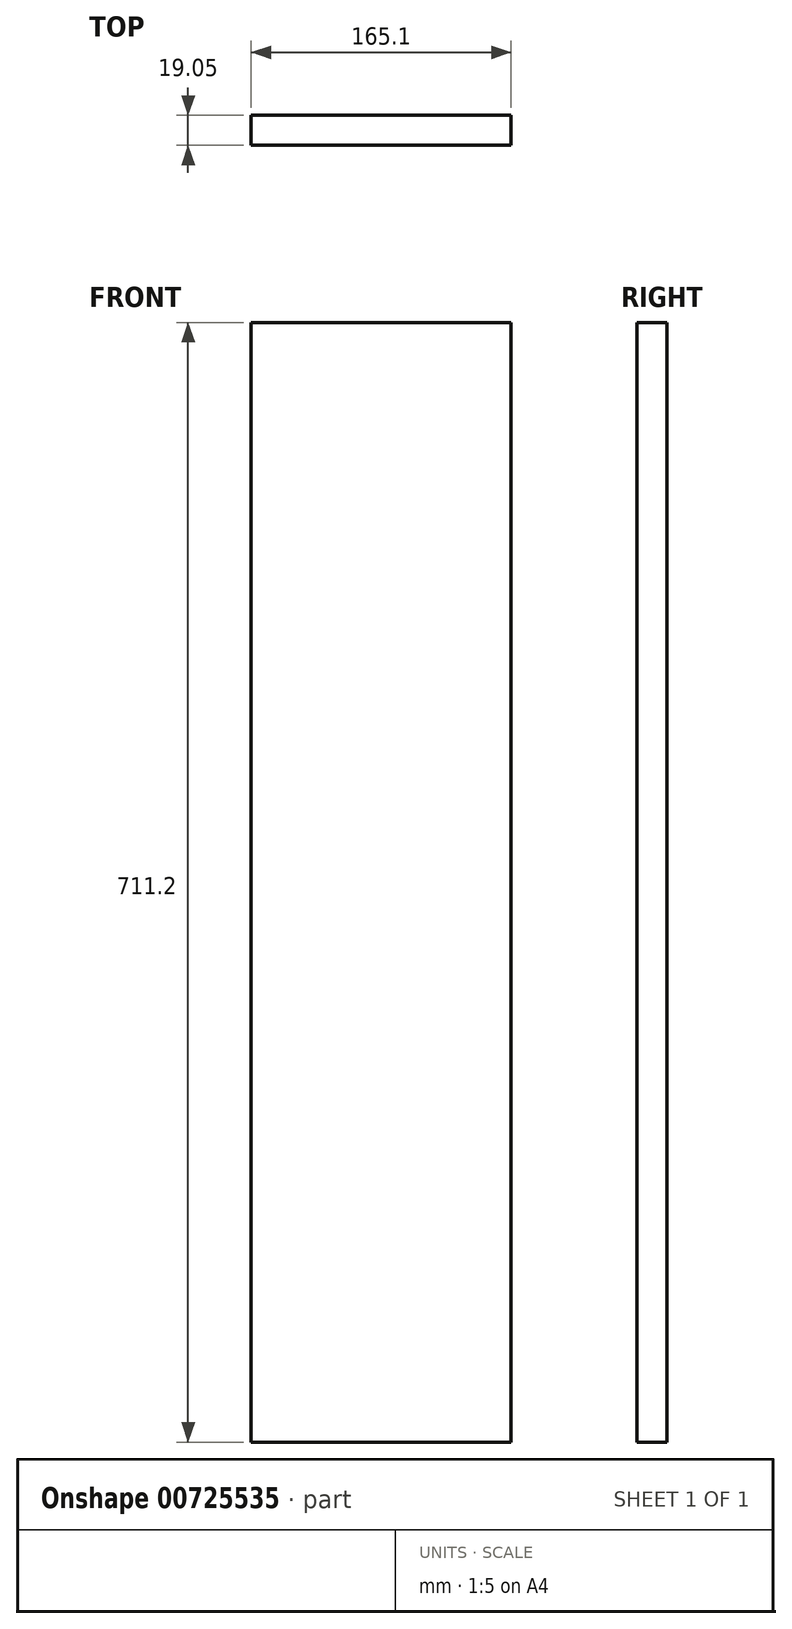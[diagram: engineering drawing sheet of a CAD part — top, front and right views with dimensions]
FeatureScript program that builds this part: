
annotation { "Feature Type Name" : "Feature", "Feature Type Description" : "" }
export const myFeature = defineFeature(function(context is Context, id is Id, definition is map)
    precondition{}
    {
        {
            var Q0;
            Q0=qCreatedBy(makeId("Front.planeOp"),FACE);
            var sketch = newSketch(context, id + "F0", { "sketchPlane" : qUnion([Q0])});
            skLineSegment(sketch, "E0.bottom", {"start": v(82.55, 355.6) * mm, "end": v(-82.55, 355.6) * mm});
            skLineSegment(sketch, "E0.top", {"start": v(82.55, -355.6) * mm, "end": v(-82.55, -355.6) * mm});
            skLineSegment(sketch, "E0.left", {"start": v(82.55, 355.6) * mm, "end": v(82.55, -355.6) * mm});
            skLineSegment(sketch, "E0.right", {"start": v(-82.55, 355.6) * mm, "end": v(-82.55, -355.6) * mm});
            skPoint(sketch, "E0.middle", {"position": v(0, 0) * mm});
            skSolve(sketch);
        }
        {
            var Q0;
            Q0=makeQuery(id+"F0.imprint","IMPRINT",FACE,{"disambiguationData":[TD([[makeQuery(id+"F0.imprint","IMPRINT",EDGE,{"derivedFrom":sQuery(id+"F0.wireOp",EDGE,"E0.bottom")}),1.0]])]});
            extrude(context, id + "F1", {"entities" : qUnion([Q0]), "depth" : 19.05 * mm, "offsetDistance" : 25.4 * mm});
        }
    });
